# Revit family: 201_PRW-598-24-B-_+NK-SWB
name_source: partatom
category: Air Terminals
units: mm (PartAtom-declared; Revit-internal decimal feet)

## family parameters
Always vertical = Yes
Cut with Voids When Loaded = No
Part Type = Normal
Room Calculation Point = Yes
Round Connector Dimension = Use Diameter
Shared = No
Work Plane-Based = No

## types (1)
- PRW-598-24-B-250+NK-SWB
    A2 = 300 mm  [stored 0.984252 ft]
    C1 = 330 mm  [stored 1.08268 ft]
    CAT0 = Yes
    CLBTZ = 0 mm  [stored 0 ft]
    CL_Location_5000 = 5000 mm  [stored 16.4042 ft]
    D = 250 mm
    DPX = 281 mm
    DPZ = 165 mm  [stored 0.541339 ft]
    DS2 = 281 mm
    DZ = 5 mm  [stored 0.0164042 ft]
    Description = EXPANSION BOXES TO BE MOUNTED UNDER THE NKSD-C, NKSD-CB, NK-SWB DIFFUSERS
    H_ARR = 0 mm  [stored 0 ft]
    L_ARR = 400 mm  [stored 1.31234 ft]
    MC Product Code = PRW-598-24-B-250+NK-SWB
    Manufacturer = Alnor
    QmdConnectorList = 201;D
    SW1 = Yes
    SW2 = No
    URL = http://www.ventilation-alnor.co.uk
    W_ARR = 400 mm  [stored 1.31234 ft]
    XRefLineVPlnId = 7453
    YRefLineVPlnId = 7456
    magiPartTypeId = 201
    magiProductFamilyId = PRW-598-24-B-*+NK-SWB
    magiProductId = PRW-598-24-B-250+NK-SWB

note: [stored X ft] marks values corroborated as IEEE doubles in the binary element streams (Revit-internal decimal feet)

## geometry (parser evidence)
native form markers: Blend x2, Sweep x2
no freeform markers — native parametric forms only
